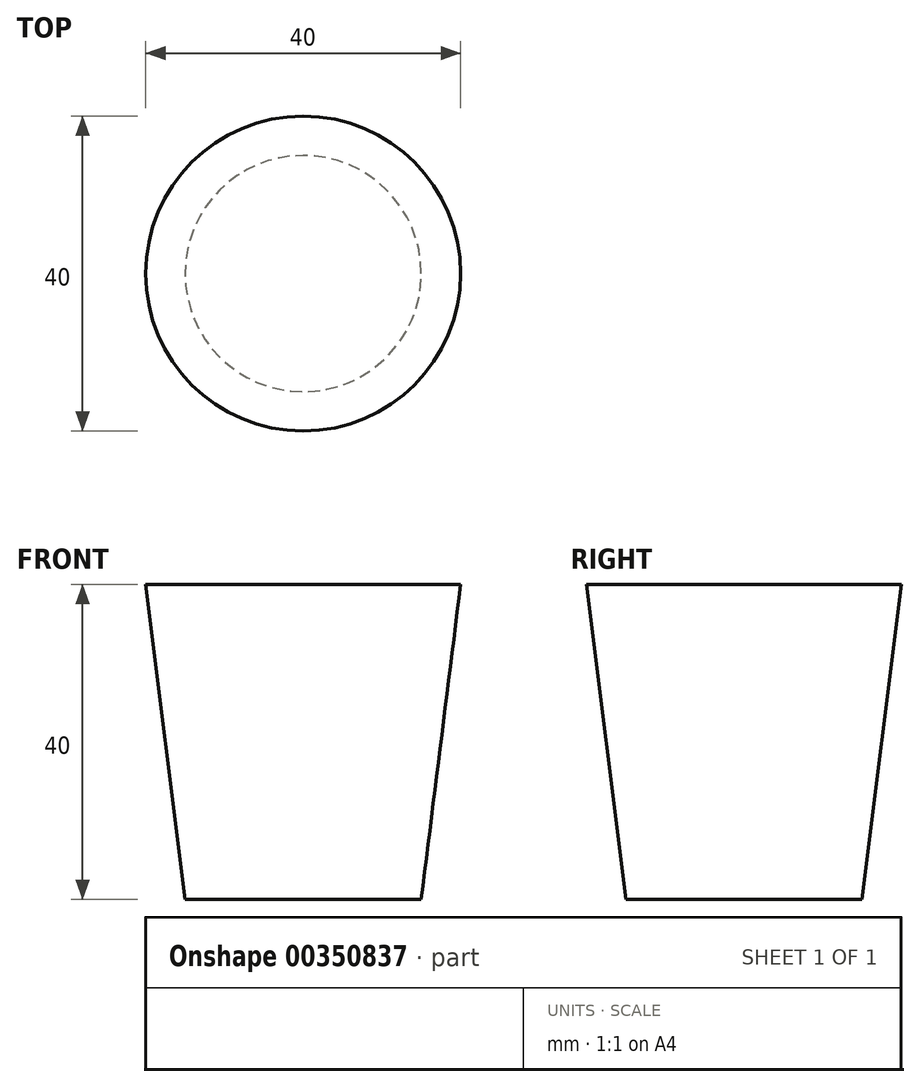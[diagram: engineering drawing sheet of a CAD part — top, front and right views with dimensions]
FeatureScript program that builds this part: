
annotation { "Feature Type Name" : "Feature", "Feature Type Description" : "" }
export const myFeature = defineFeature(function(context is Context, id is Id, definition is map)
    precondition{}
    {
        {
            var Q0;
            Q0=qCreatedBy(makeId("Top.planeOp"),FACE);
            var sketch = newSketch(context, id + "F0", { "sketchPlane" : qUnion([Q0])});
            skCircle(sketch, "E0", {"center": v(0, 0) * mm, "radius": 20 * mm});
            skSolve(sketch);
        }
        {
            var Q0;
            Q0 = qSketchRegion(id + "F0", true);
            extrude(context, id + "F1", {"entities" : qUnion([Q0]), "depth" : 40 * mm});
        }
        {
            var Q0;
            Q0=makeQuery(id+"F1.opExtrude","CAP_EDGE",EDGE,{"disambiguationData":[OSD([sQuery(id+"F0.wireOp",EDGE,"E0")])],"isStart":true});
            chamfer(context, id + "F2", {"entities" : qUnion([Q0]), "chamferType" : ChamferType.TWO_OFFSETS, "width1" : 40 * mm, "oppositeDirection" : false, "width2" : 5 * mm, "tangentPropagation" : true});
        }
    });
